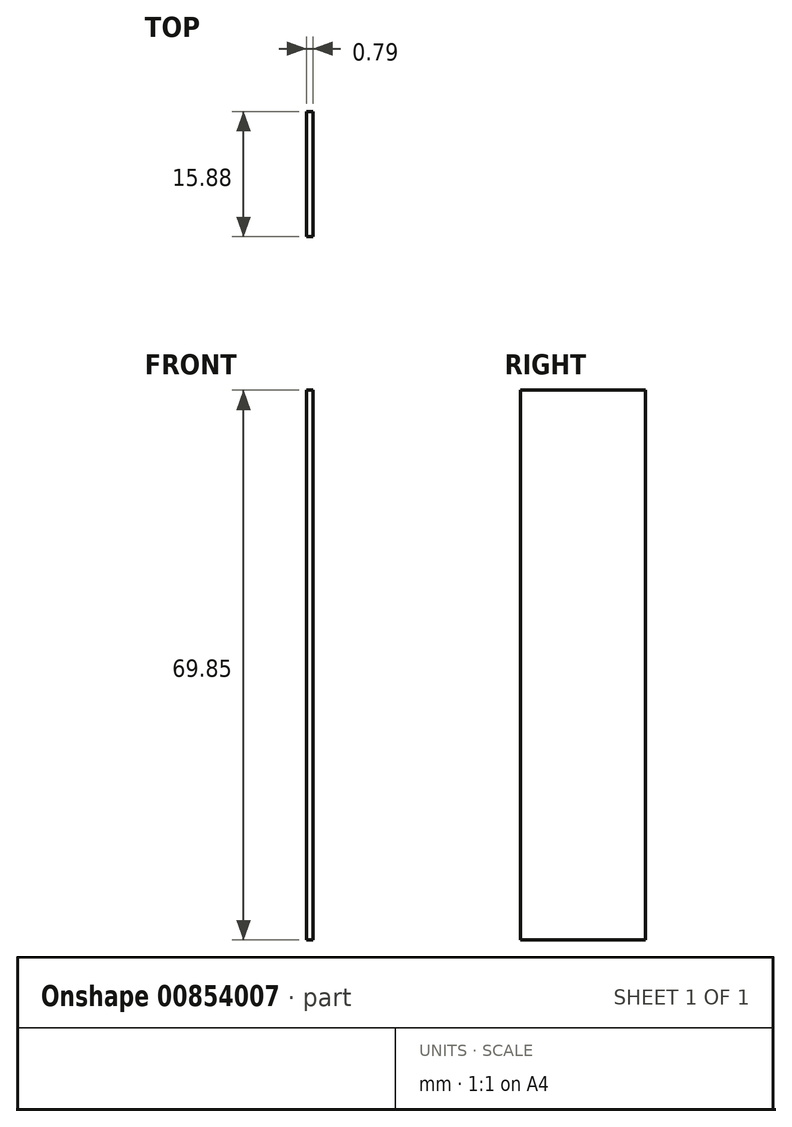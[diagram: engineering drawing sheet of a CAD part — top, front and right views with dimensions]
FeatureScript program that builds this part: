
annotation { "Feature Type Name" : "Feature", "Feature Type Description" : "" }
export const myFeature = defineFeature(function(context is Context, id is Id, definition is map)
    precondition{}
    {
        {
            var Q0;
            Q0=qCreatedBy(makeId("Front.planeOp"),FACE);
            var sketch = newSketch(context, id + "F0", { "sketchPlane" : qUnion([Q0])});
            skLineSegment(sketch, "E0.bottom", {"start": v(0, 69.85) * mm, "end": v(0.8, 69.85) * mm});
            skLineSegment(sketch, "E0.top", {"start": v(0, 0) * mm, "end": v(0.8, 0) * mm});
            skLineSegment(sketch, "E0.left", {"start": v(0, 69.85) * mm, "end": v(0, 0) * mm});
            skLineSegment(sketch, "E0.right", {"start": v(0.8, 69.85) * mm, "end": v(0.8, 0) * mm});
            skSolve(sketch);
        }
        {
            var Q0;
            Q0=makeQuery(id+"F0.imprint","IMPRINT",FACE,{"disambiguationData":[TD([[makeQuery(id+"F0.imprint","IMPRINT",EDGE,{"derivedFrom":sQuery(id+"F0.wireOp",EDGE,"E0.bottom")}),-1.0]])]});
            extrude(context, id + "F1", {"entities" : qUnion([Q0]), "oppositeDirection" : true, "depth" : 15.88 * mm, "offsetDistance" : 25.4 * mm});
        }
    });
